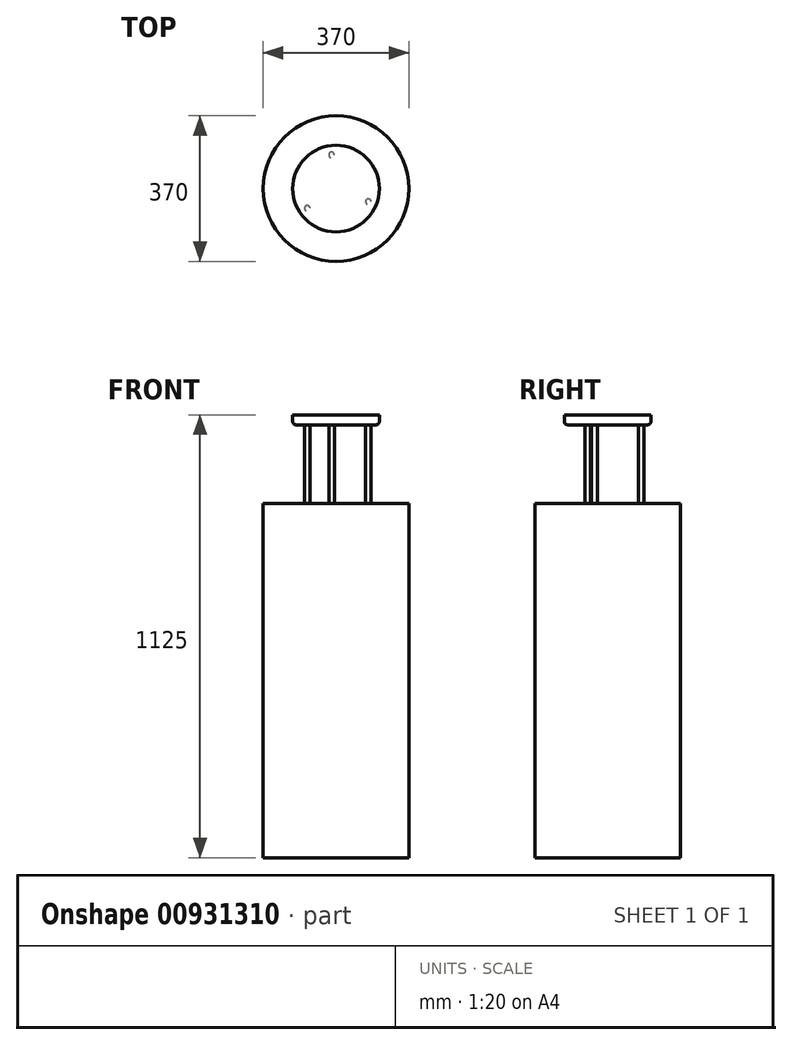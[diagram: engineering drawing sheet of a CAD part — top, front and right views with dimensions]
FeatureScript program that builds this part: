
annotation { "Feature Type Name" : "Feature", "Feature Type Description" : "" }
export const myFeature = defineFeature(function(context is Context, id is Id, definition is map)
    precondition{}
    {
        {
            var Q0;
            Q0=qCreatedBy(makeId("Top.planeOp"),FACE);
            var sketch = newSketch(context, id + "F0", { "sketchPlane" : qUnion([Q0])});
            skCircle(sketch, "E0", {"center": v(0, 0) * mm, "radius": 185 * mm});
            skSolve(sketch);
        }
        {
            var Q0;
            Q0=makeQuery(id+"F0.imprint","IMPRINT",FACE,{"disambiguationData":[TD([[makeQuery(id+"F0.imprint","IMPRINT",EDGE,{"derivedFrom":sQuery(id+"F0.wireOp",EDGE,"E0")}),1.0]])]});
            extrude(context, id + "F1", {"entities" : qUnion([Q0]), "depth" : 900 * mm, "offsetDistance" : 25 * mm});
        }
        {
            var Q0;
            Q0=makeQuery(id+"F1.opExtrude","CAP_FACE",FACE,{"disambiguationData":[OSD([sQuery(id+"F0.wireOp",EDGE,"E0")])],"isStart":false});
            var sketch = newSketch(context, id + "F2", { "sketchPlane" : qUnion([Q0])});
            skCircle(sketch, "E1", {"center": v(0, 0) * mm, "radius": 87.5 * mm});
            skSolve(sketch);
        }
        {
            var Q0;
            Q0=makeQuery(id+"F2.imprint","IMPRINT",FACE,{"disambiguationData":[TD([[makeQuery(id+"F2.imprint","IMPRINT",EDGE,{"derivedFrom":sQuery(id+"F2.wireOp",EDGE,"E1")}),-1.0]])]});
            var sketch = newSketch(context, id + "F3", { "sketchPlane" : qUnion([Q0])});
            skCircle(sketch, "E2", {"center": v(-73.03, -49.98) * mm, "radius": 7 * mm});
            skCircle(sketch, "E3", {"center": v(-11.36, 85.57) * mm, "radius": 7 * mm});
            skCircle(sketch, "E4", {"center": v(82.27, -33.38) * mm, "radius": 7 * mm});
            skSolve(sketch);
        }
        {
            var Q0;
            {var subQ0=sQuery(id+"F3.wireOp",EDGE,"E4");var subQ1=makeQuery(id+"F2.imprint","IMPRINT",EDGE,{"derivedFrom":sQuery(id+"F2.wireOp",EDGE,"E1")});var subQ2=makeQuery(id+"F3.imprint","INTERSECT",VERTEX,{"disambiguationData":[OD(0.0)],"derivedFrom":[subQ1,subQ0]});Q0=makeQuery(id+"F3.imprint","IMPRINT",FACE,{"disambiguationData":[TD([[makeQuery(id+"F3.imprint","IMPRINT",EDGE,{"disambiguationData":[TD([[subQ2,-1.0]])],"derivedFrom":subQ0}),1.0]])]});}
            var Q1;
            {var subQ0=sQuery(id+"F3.wireOp",EDGE,"E4");var subQ1=makeQuery(id+"F2.imprint","IMPRINT",EDGE,{"derivedFrom":sQuery(id+"F2.wireOp",EDGE,"E1")});var subQ2=makeQuery(id+"F3.imprint","INTERSECT",VERTEX,{"disambiguationData":[OD(0.0)],"derivedFrom":[subQ1,subQ0]});Q1=makeQuery(id+"F3.imprint","IMPRINT",FACE,{"disambiguationData":[TD([[makeQuery(id+"F3.imprint","IMPRINT",EDGE,{"disambiguationData":[TD([[subQ2,1.0]])],"derivedFrom":subQ0}),1.0]])]});}
            var Q2;
            {var subQ0=sQuery(id+"F3.wireOp",EDGE,"E2");var subQ1=makeQuery(id+"F2.imprint","IMPRINT",EDGE,{"derivedFrom":sQuery(id+"F2.wireOp",EDGE,"E1")});var subQ2=makeQuery(id+"F3.imprint","INTERSECT",VERTEX,{"disambiguationData":[OD(0.0)],"derivedFrom":[subQ1,subQ0]});Q2=makeQuery(id+"F3.imprint","IMPRINT",FACE,{"disambiguationData":[TD([[makeQuery(id+"F3.imprint","IMPRINT",EDGE,{"disambiguationData":[TD([[subQ2,1.0]])],"derivedFrom":subQ0}),1.0]])]});}
            var Q3;
            {var subQ0=sQuery(id+"F3.wireOp",EDGE,"E2");var subQ1=makeQuery(id+"F2.imprint","IMPRINT",EDGE,{"derivedFrom":sQuery(id+"F2.wireOp",EDGE,"E1")});var subQ2=makeQuery(id+"F3.imprint","INTERSECT",VERTEX,{"disambiguationData":[OD(0.0)],"derivedFrom":[subQ1,subQ0]});Q3=makeQuery(id+"F3.imprint","IMPRINT",FACE,{"disambiguationData":[TD([[makeQuery(id+"F3.imprint","IMPRINT",EDGE,{"disambiguationData":[TD([[subQ2,-1.0]])],"derivedFrom":subQ0}),1.0]])]});}
            var Q4;
            {var subQ0=sQuery(id+"F3.wireOp",EDGE,"E3");var subQ1=makeQuery(id+"F2.imprint","IMPRINT",EDGE,{"derivedFrom":sQuery(id+"F2.wireOp",EDGE,"E1")});var subQ2=makeQuery(id+"F3.imprint","INTERSECT",VERTEX,{"disambiguationData":[OD(0.0)],"derivedFrom":[subQ1,subQ0]});Q4=makeQuery(id+"F3.imprint","IMPRINT",FACE,{"disambiguationData":[TD([[makeQuery(id+"F3.imprint","IMPRINT",EDGE,{"disambiguationData":[TD([[subQ2,-1.0]])],"derivedFrom":subQ0}),1.0]])]});}
            var Q5;
            {var subQ0=sQuery(id+"F3.wireOp",EDGE,"E3");var subQ1=makeQuery(id+"F2.imprint","IMPRINT",EDGE,{"derivedFrom":sQuery(id+"F2.wireOp",EDGE,"E1")});var subQ2=makeQuery(id+"F3.imprint","INTERSECT",VERTEX,{"disambiguationData":[OD(0.0)],"derivedFrom":[subQ1,subQ0]});Q5=makeQuery(id+"F3.imprint","IMPRINT",FACE,{"disambiguationData":[TD([[makeQuery(id+"F3.imprint","IMPRINT",EDGE,{"disambiguationData":[TD([[subQ2,1.0]])],"derivedFrom":subQ0}),1.0]])]});}
            extrude(context, id + "F4", {"entities" : qUnion([Q0, Q1, Q2, Q3, Q4, Q5]), "operationType" : NewBodyOperationType.ADD, "depth" : 200 * mm, "offsetDistance" : 25 * mm});
        }
        {
            var Q0;
            Q0=makeQuery(id+"F4.opExtrude","CAP_FACE",FACE,{"disambiguationData":[OSD([sQuery(id+"F3.wireOp",EDGE,"E3")])],"isStart":false});
            var sketch = newSketch(context, id + "F5", { "sketchPlane" : qUnion([Q0])});
            skPoint(sketch, "E5.0", {"position": v(0, 0) * mm});
            skCircle(sketch, "E6", {"center": v(0, 0) * mm, "radius": 110 * mm});
            skSolve(sketch);
        }
        {
            var Q0;
            Q0=makeQuery(id+"F5.imprint","IMPRINT",FACE,{"disambiguationData":[TD([[makeQuery(id+"F5.imprint","IMPRINT",EDGE,{"derivedFrom":sQuery(id+"F5.wireOp",EDGE,"E6")}),1.0]])]});
            var Q1;
            Q1=makeQuery(id+"F5.imprint","IMPRINT",FACE,{"disambiguationData":[TD([[makeQuery(id+"F5.imprint","IMPRINT",EDGE,{"derivedFrom":makeQuery(id+"F4.opExtrude","CAP_EDGE",EDGE,{"disambiguationData":[OSD([sQuery(id+"F3.wireOp",EDGE,"E3")])],"isStart":false})}),1.0]])]});
            extrude(context, id + "F6", {"entities" : qUnion([Q0, Q1]), "operationType" : NewBodyOperationType.ADD, "depth" : 25 * mm, "offsetDistance" : 25 * mm});
        }
        {
            var Q0;
            Q0=makeQuery(id+"F6.opExtrude","CAP_EDGE",EDGE,{"disambiguationData":[OSD([sQuery(id+"F5.wireOp",EDGE,"E6")])],"isStart":true});
            fillet(context, id + "F7", {"entities" : qUnion([Q0]), "radius" : 8 * mm, "tangentPropagation" : true, "allowEdgeOverflow" : false});
        }
    });
